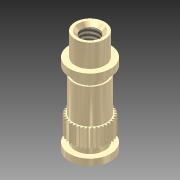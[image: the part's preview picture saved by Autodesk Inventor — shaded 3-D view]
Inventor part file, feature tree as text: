
AUTODESK INVENTOR PART (.ipt)
format: ipt  version: 2014 SP1 (Build 180222100, 222)  size: 245,760 bytes
history: native  units: in
note: dims shown in document units (in); Inventor stores cm internally (conversion verified against a paired STEP export)
features: other x1, imported_body x1, thread x1
ambient origin geometry x8: Origin, YZ Plane, XZ Plane, XY Plane, X Axis, Y Axis, Z Axis, Center Point
bodies: Body1 (feature_tree)
feature tree (3):
  parser-record x1  (decoder bookkeeping rows leaked as tree rows — omitted from the tree; the rows remain in map.json)
  imported_body  "Base1"
  thread  "Thread1"  [1 undecoded]
note: 1 required parameter value undecoded (feature->parameter linkage not recoverable at this tier; creation-order binding heuristic only, values carry confidence <= 0.55)
